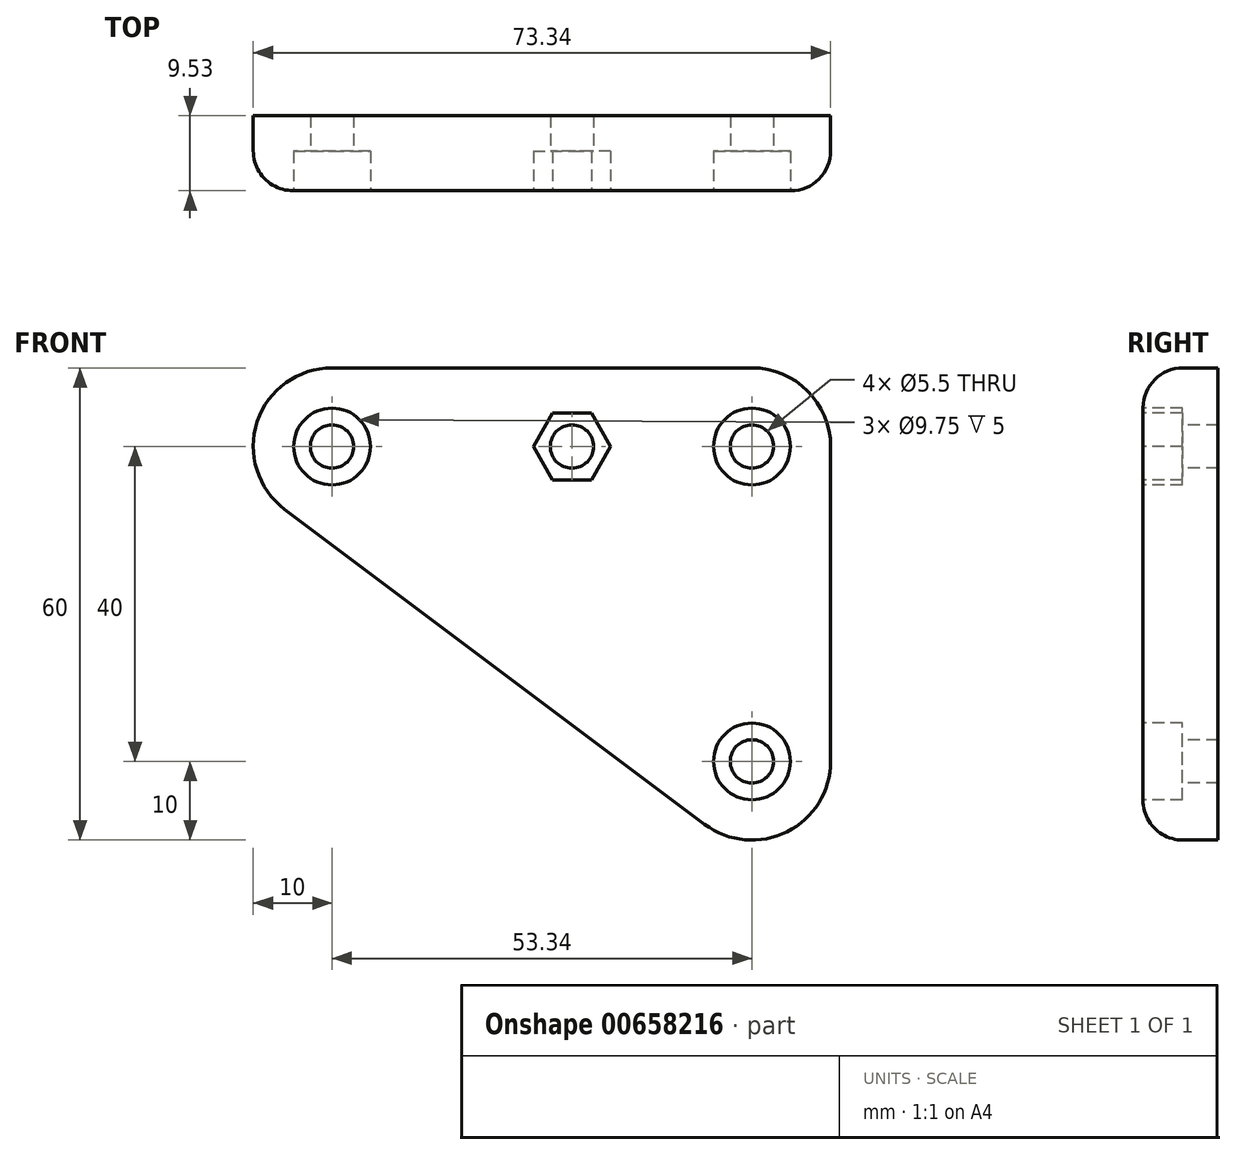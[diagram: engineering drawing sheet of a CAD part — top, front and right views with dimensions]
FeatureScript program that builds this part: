
annotation { "Feature Type Name" : "Feature", "Feature Type Description" : "" }
export const myFeature = defineFeature(function(context is Context, id is Id, definition is map)
    precondition{}
    {
        {
            var Q0;
            Q0=qCreatedBy(makeId("Front.planeOp"),FACE);
            var sketch = newSketch(context, id + "F0", { "sketchPlane" : qUnion([Q0])});
            skPoint(sketch, "E0", {"position": v(-22.86, 0) * mm});
            skArc(sketch, "E1", {"start": v(10, 0) * mm, "mid": v(7.07, 7.07) * mm, "end": v(0, 10) * mm});
            skPoint(sketch, "E2", {"position": v(0, -40) * mm});
            skArc(sketch, "E3", {"start": v(-6, -48) * mm, "mid": v(4.47, -48.94) * mm, "end": v(10, -40) * mm});
            skArc(sketch, "E4", {"start": v(-53.34, 10) * mm, "mid": v(-62.83, 3.16) * mm, "end": v(-59.34, -8) * mm});
            skLineSegment(sketch, "E5", {"start": v(-59.34, -8) * mm, "end": v(-6, -48) * mm});
            skLineSegment(sketch, "E6", {"start": v(-53.34, 10) * mm, "end": v(0, 10) * mm});
            skLineSegment(sketch, "E7", {"start": v(10, -40) * mm, "end": v(10, 0) * mm});
            skCircle(sketch, "E8.cCircle", {"center": v(-22.86, 0) * mm, "radius": 4.25 * mm, "construction": true});
            skLineSegment(sketch, "E8.0", {"start": v(-20.4, -4.25) * mm, "end": v(-25.31, -4.25) * mm});
            skLineSegment(sketch, "E8.1", {"start": v(-25.31, -4.25) * mm, "end": v(-27.77, 0) * mm});
            skLineSegment(sketch, "E8.2", {"start": v(-27.77, 0) * mm, "end": v(-25.31, 4.25) * mm});
            skLineSegment(sketch, "E8.3", {"start": v(-25.31, 4.25) * mm, "end": v(-20.4, 4.25) * mm});
            skLineSegment(sketch, "E8.4", {"start": v(-20.4, 4.25) * mm, "end": v(-17.95, 0) * mm});
            skLineSegment(sketch, "E8.5", {"start": v(-17.95, 0) * mm, "end": v(-20.4, -4.25) * mm});
            skPoint(sketch, "E8.0.midPoint", {"position": v(-22.86, -4.25) * mm});
            skSolve(sketch);
        }
        {
            var Q0;
            Q0=makeQuery(id+"F0.imprint","IMPRINT",FACE,{"disambiguationData":[TD([[makeQuery(id+"F0.imprint","IMPRINT",EDGE,{"derivedFrom":sQuery(id+"F0.wireOp",EDGE,"E1")}),1.0]])]});
            var Q1;
            Q1=makeQuery(id+"F0.imprint","IMPRINT",FACE,{"disambiguationData":[TD([[makeQuery(id+"F0.imprint","IMPRINT",EDGE,{"derivedFrom":sQuery(id+"F0.wireOp",EDGE,"E8.0")}),-1.0]])]});
            extrude(context, id + "F1", {"entities" : qUnion([Q0, Q1]), "oppositeDirection" : true, "depth" : 9.52 * mm, "offsetDistance" : 25.4 * mm});
        }
        {
            var Q0;
            Q0=sQuery(id+"F0.wireOp",VERTEX,"E1.center");
            var Q1;
            Q1=sQuery(id+"F0.wireOp",VERTEX,"E2");
            var Q2;
            Q2=sQuery(id+"F0.wireOp",VERTEX,"f07db37f-82a6-4f9c-b0d2-fdbc7351bc77.MirrorP");
            var Q3;
            Q3=sQuery(id+"F0.wireOp",VERTEX,"E4.center");
            var Q4;
            Q4=makeQuery(id+"F1.opExtrude","SWEPT_BODY",BODY,{"disambiguationData":[OSD([sQuery(id+"F0.wireOp",EDGE,"bf2f238d-4e1d-4e86-ab75-1465cd813df2.MirrorCS"),sQuery(id+"F0.wireOp",EDGE,"7d5bedbb-471c-4160-8e68-eb1f4d767648.MirrorCS"),sQuery(id+"F0.wireOp",EDGE,"bc7fee83-9e46-4c51-805a-8ae9689402aa.MirrorCS"),sQuery(id+"F0.wireOp",EDGE,"e5d497b7-cccf-4703-a1dc-18e520bbeae9.MirrorCS"),sQuery(id+"F0.wireOp",EDGE,"c155fd9a-5cc5-4759-a1c6-071fd15af197.MirrorCS"),sQuery(id+"F0.wireOp",EDGE,"33a989d6-5cc4-4172-ab73-ca817da9f412.MirrorCS"),sQuery(id+"F0.wireOp",EDGE,"1c3aec17-fec7-453e-8acd-3df81b9bc4e3.MirrorCS"),sQuery(id+"F0.wireOp",EDGE,"0cd19f4d-6d86-4b4a-a093-bb589b475590.MirrorCS"),sQuery(id+"F0.wireOp",EDGE,"eee5d6f5-912f-4719-99ba-1d72e724f1e9.MirrorCS"),sQuery(id+"F0.wireOp",EDGE,"64a401ff-d109-42b1-96b9-6f7f2e519c4d.MirrorCS"),sQuery(id+"F0.wireOp",EDGE,"2bc110f3-ae92-45de-b2b7-7df43831b8ab"),sQuery(id+"F0.wireOp",EDGE,"pibmvETk-c1Xj-BIgN-8uma-1jo4IxxjolSW")])]});
            var Q5;
            Q5=makeQuery(id+"F1.opExtrude","SWEPT_BODY",BODY,{"disambiguationData":[OSD([sQuery(id+"F0.wireOp",EDGE,"E1"),sQuery(id+"F0.wireOp",EDGE,"E3"),sQuery(id+"F0.wireOp",EDGE,"E4"),sQuery(id+"F0.wireOp",EDGE,"E5"),sQuery(id+"F0.wireOp",EDGE,"E6"),sQuery(id+"F0.wireOp",EDGE,"E7"),sQuery(id+"F0.wireOp",EDGE,"abe57e29-0c7c-4b99-905f-2de660d06fb5.0"),sQuery(id+"F0.wireOp",EDGE,"3414c082-77eb-4b60-8568-4fb26c363dc8.0"),sQuery(id+"F0.wireOp",EDGE,"de1da2a2-a23f-4f41-af84-cb727b929bf4.0"),sQuery(id+"F0.wireOp",EDGE,"a5e2c965-bc7c-4ac8-a8c3-57b03be74d22.filletArc"),sQuery(id+"F0.wireOp",EDGE,"b6b388fa-fd1b-47d1-968e-da1be4f55a76.filletArc"),sQuery(id+"F0.wireOp",EDGE,"61007793-95a0-45a8-9965-7a1efe876f03.filletArc")])]});
            hole(context, id + "F2", {"style" : HoleStyle.C_BORE, "endStyle" : HoleEndStyle.THROUGH, "standardTappedOrClearance" : lookupTablePath({ "standard" : "ISO", "fit" : "Normal", "size" : "M5", "type" : "Clearance" }), "standardBlindInLast" : lookupTablePath({ "fit" : "Standard", "standard" : "ISO", "size" : "M5", "type" : "Clearance" }), "holeDiameter" : 5.5 * mm, "cBoreDiameter" : 9.75 * mm, "cBoreDepth" : 5 * mm, "majorDiameter" : 6.35 * mm, "isTappedThrough" : true, "tappedDepth" : 12.7 * mm, "tapClearance" : 3, "locations" : qUnion([Q0, Q1, Q2, Q3]), "scope" : qUnion([Q4, Q5])});
        }
        {
            var Q0;
            Q0=makeQuery(id+"F1.opExtrude","CAP_EDGE",EDGE,{"disambiguationData":[OSD([sQuery(id+"F0.wireOp",EDGE,"E6")])],"isStart":true});
            var Q1;
            Q1=makeQuery(id+"F1.opExtrude","CAP_EDGE",EDGE,{"disambiguationData":[OSD([sQuery(id+"F0.wireOp",EDGE,"de1da2a2-a23f-4f41-af84-cb727b929bf4.0")])],"isStart":true});
            fillet(context, id + "F3", {"entities" : qUnion([Q0, Q1]), "radius" : 5.08 * mm, "tangentPropagation" : true, "allowEdgeOverflow" : false});
        }
        {
            var Q0;
            Q0=makeQuery(id+"F0.imprint","IMPRINT",FACE,{"disambiguationData":[TD([[makeQuery(id+"F0.imprint","IMPRINT",EDGE,{"derivedFrom":sQuery(id+"F0.wireOp",EDGE,"E8.0")}),-1.0]])]});
            extrude(context, id + "F4", {"entities" : qUnion([Q0]), "operationType" : NewBodyOperationType.REMOVE, "oppositeDirection" : true, "depth" : 5 * mm, "offsetDistance" : 25.4 * mm});
        }
        {
            var Q0;
            Q0=sQuery(id+"F0.wireOp",VERTEX,"E0");
            var Q1;
            Q1=makeQuery(id+"F1.opExtrude","SWEPT_BODY",BODY,{"disambiguationData":[OSD([sQuery(id+"F0.wireOp",EDGE,"E1"),sQuery(id+"F0.wireOp",EDGE,"E3"),sQuery(id+"F0.wireOp",EDGE,"E4"),sQuery(id+"F0.wireOp",EDGE,"E5"),sQuery(id+"F0.wireOp",EDGE,"E6"),sQuery(id+"F0.wireOp",EDGE,"E7")])]});
            hole(context, id + "F5", {"style" : HoleStyle.SIMPLE, "endStyle" : HoleEndStyle.THROUGH, "standardTappedOrClearance" : lookupTablePath({ "standard" : "ISO", "fit" : "Normal", "size" : "M5", "type" : "Clearance" }), "standardBlindInLast" : lookupTablePath({ "fit" : "Standard", "standard" : "ISO", "size" : "M5", "type" : "Clearance" }), "holeDiameter" : 5.5 * mm, "majorDiameter" : 6.35 * mm, "isTappedThrough" : true, "tappedDepth" : 12.7 * mm, "tapClearance" : 3, "locations" : qUnion([Q0]), "scope" : qUnion([Q1])});
        }
    });
